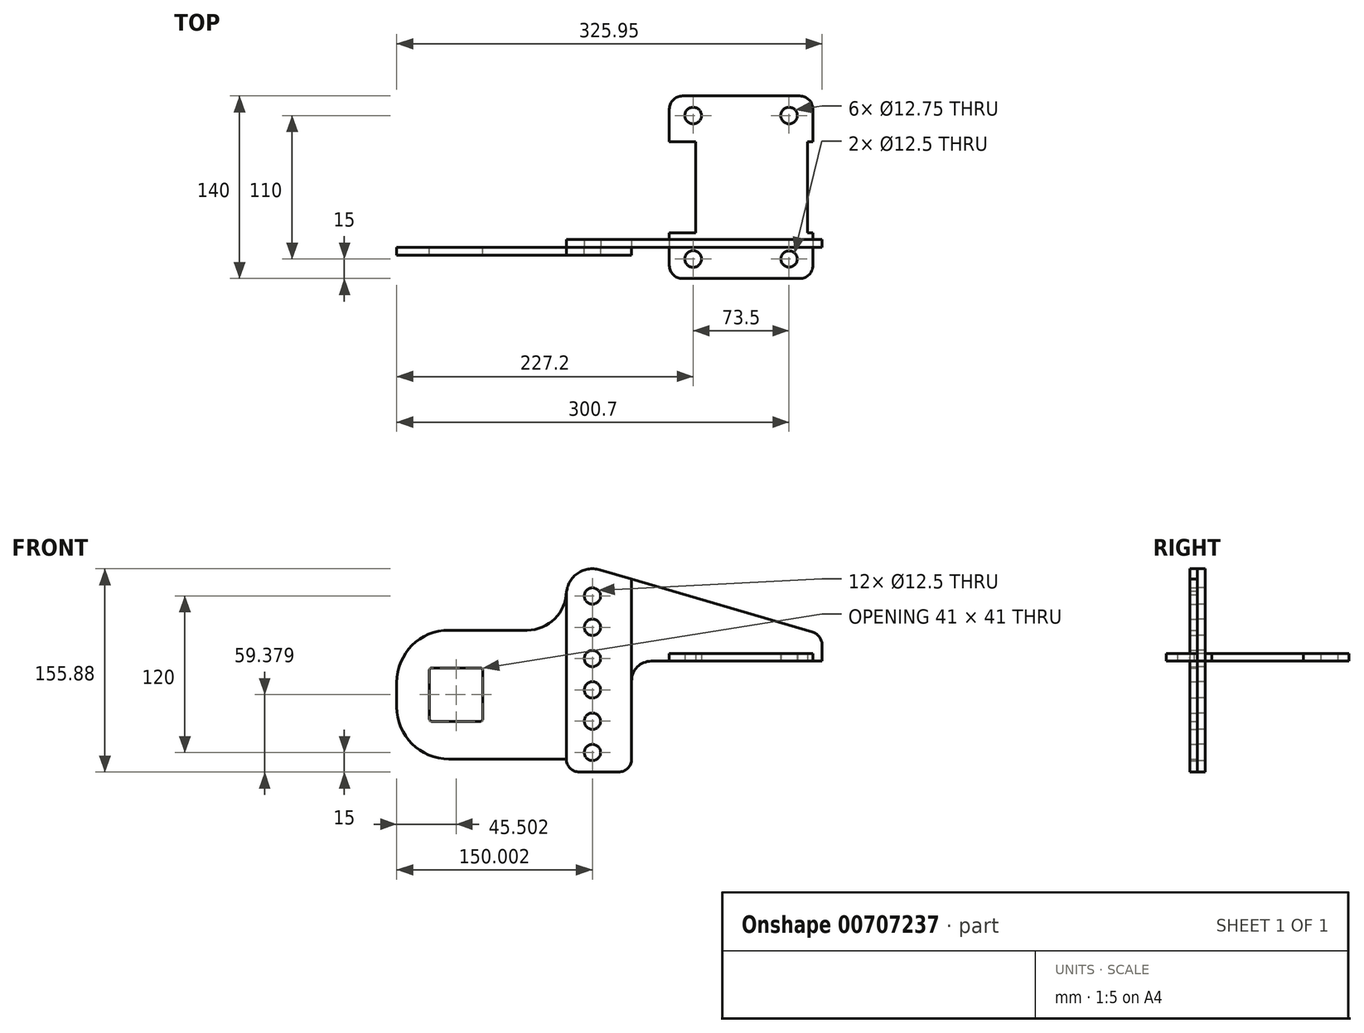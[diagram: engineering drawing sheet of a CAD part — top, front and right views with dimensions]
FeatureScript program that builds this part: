
annotation { "Feature Type Name" : "Feature", "Feature Type Description" : "" }
export const myFeature = defineFeature(function(context is Context, id is Id, definition is map)
    precondition{}
    {
        {
            var Q0;
            Q0=qCreatedBy(makeId("Top.planeOp"),FACE);
            var sketch = newSketch(context, id + "F0", { "sketchPlane" : qUnion([Q0])});
            skLineSegment(sketch, "E0.bottom", {"start": v(36.75, -55) * mm, "end": v(-36.75, -55) * mm, "construction": true});
            skLineSegment(sketch, "E0.top", {"start": v(36.75, 55) * mm, "end": v(-36.75, 55) * mm, "construction": true});
            skLineSegment(sketch, "E0.left", {"start": v(36.75, -55) * mm, "end": v(36.75, 55) * mm, "construction": true});
            skLineSegment(sketch, "E0.right", {"start": v(-36.75, -55) * mm, "end": v(-36.75, 55) * mm, "construction": true});
            skPoint(sketch, "E0.middle", {"position": v(0, 0) * mm});
            skCircle(sketch, "E1", {"center": v(-36.75, 55) * mm, "radius": 6.38 * mm});
            skCircle(sketch, "E2", {"center": v(36.75, 55) * mm, "radius": 6.38 * mm});
            skCircle(sketch, "E3", {"center": v(-36.75, -55) * mm, "radius": 6.38 * mm});
            skCircle(sketch, "E4", {"center": v(36.75, -55) * mm, "radius": 6.25 * mm});
            skLineSegment(sketch, "E5.bottom", {"start": v(45, 70) * mm, "end": v(-45, 70) * mm});
            skLineSegment(sketch, "E5.top", {"start": v(45, -70) * mm, "end": v(-45, -70) * mm});
            skLineSegment(sketch, "E5.left", {"start": v(55, 60) * mm, "end": v(55, 35) * mm});
            skLineSegment(sketch, "E5.right", {"start": v(-55, 60) * mm, "end": v(-55, 35) * mm});
            skPoint(sketch, "E6.visualSharp", {"position": v(-55, -70) * mm});
            skArc(sketch, "E6.filletArc", {"start": v(-55, -60) * mm, "mid": v(-52.07, -67.07) * mm, "end": v(-45, -70) * mm});
            skPoint(sketch, "E7.visualSharp", {"position": v(-55, 70) * mm});
            skArc(sketch, "E7.filletArc", {"start": v(-45, 70) * mm, "mid": v(-52.07, 67.07) * mm, "end": v(-55, 60) * mm});
            skPoint(sketch, "E8.visualSharp", {"position": v(55, 70) * mm});
            skArc(sketch, "E8.filletArc", {"start": v(55, 60) * mm, "mid": v(52.07, 67.07) * mm, "end": v(45, 70) * mm});
            skPoint(sketch, "E9.visualSharp", {"position": v(55, -70) * mm});
            skArc(sketch, "E9.filletArc", {"start": v(45, -70) * mm, "mid": v(52.07, -67.07) * mm, "end": v(55, -60) * mm});
            skLineSegment(sketch, "E10", {"start": v(-35, 0) * mm, "end": v(-35, -35) * mm});
            skLineSegment(sketch, "E11", {"start": v(-35, -35) * mm, "end": v(-55, -35) * mm});
            skLineSegment(sketch, "E12", {"start": v(-35, 0) * mm, "end": v(-35, 35) * mm});
            skLineSegment(sketch, "E13", {"start": v(-35, 35) * mm, "end": v(-55, 35) * mm});
            skLineSegment(sketch, "E14", {"start": v(-35, -35) * mm, "end": v(55, -35) * mm, "construction": true});
            skLineSegment(sketch, "E15", {"start": v(-35, 35) * mm, "end": v(55, 35) * mm, "construction": true});
            skLineSegment(sketch, "E16", {"start": v(55, -35) * mm, "end": v(51, -35) * mm});
            skLineSegment(sketch, "E17", {"start": v(51, -35) * mm, "end": v(51, 35) * mm});
            skLineSegment(sketch, "E18", {"start": v(51, 35) * mm, "end": v(55, 35) * mm});
            skLineSegment(sketch, "E19.trimOffspring", {"start": v(55, -35) * mm, "end": v(55, -60) * mm});
            skLineSegment(sketch, "E20.trimOffspring", {"start": v(-55, -35) * mm, "end": v(-55, -60) * mm});
            skPoint(sketch, "E21.orphan", {"position": v(-55, 0) * mm});
            skSolve(sketch);
        }
        {
            var Q0;
            Q0 = qSketchRegion(id + "F0", true);
            extrude(context, id + "F1", {"entities" : qUnion([Q0]), "depth" : 6 * mm, "offsetDistance" : 25 * mm});
        }
        {
            var Q0;
            Q0=qCreatedBy(makeId("Front.planeOp"),FACE);
            cPlane(context, id + "F2", {"entities" : qUnion([Q0]), "cplaneType" : CPlaneType.OFFSET, "offset" : 46 * mm, "width" : 150 * mm, "height" : 150 * mm});
        }
        {
            var Q0;
            Q0=qCreatedBy(id+"F2.planeOp",FACE);
            var sketch = newSketch(context, id + "F3", { "sketchPlane" : qUnion([Q0])});
            skLineSegment(sketch, "E22", {"start": v(-55, 6) * mm, "end": v(55, 6) * mm});
            skLineSegment(sketch, "E23", {"start": v(55, 6) * mm, "end": v(55, 0) * mm});
            skLineSegment(sketch, "E24", {"start": v(55, 0) * mm, "end": v(62, 0.14) * mm});
            skLineSegment(sketch, "E25", {"start": v(62, 0.14) * mm, "end": v(62, 12.65) * mm});
            skLineSegment(sketch, "E26", {"start": v(-83.95, -15) * mm, "end": v(-83.95, -75) * mm});
            skLineSegment(sketch, "E27", {"start": v(-93.95, -85) * mm, "end": v(-123.95, -85) * mm});
            skLineSegment(sketch, "E28", {"start": v(-133.95, -75) * mm, "end": v(-133.95, 50.88) * mm});
            skLineSegment(sketch, "E29", {"start": v(-108.32, 70.07) * mm, "end": v(54.81, 22.24) * mm});
            skLineSegment(sketch, "E30", {"start": v(-113.95, -85) * mm, "end": v(-113.95, 71.72) * mm, "construction": true});
            skCircle(sketch, "E31", {"center": v(-113.95, -70) * mm, "radius": 6.25 * mm});
            skCircle(sketch, "E32", {"center": v(-113.95, -46) * mm, "radius": 6.25 * mm});
            skCircle(sketch, "E33", {"center": v(-113.95, -22) * mm, "radius": 6.25 * mm});
            skCircle(sketch, "E34", {"center": v(-113.95, 2) * mm, "radius": 6.25 * mm});
            skCircle(sketch, "E35", {"center": v(-113.95, 26) * mm, "radius": 6.25 * mm});
            skCircle(sketch, "E36", {"center": v(-113.95, 50) * mm, "radius": 6.25 * mm});
            skPoint(sketch, "E37.visualSharp", {"position": v(-133.95, 77.59) * mm});
            skArc(sketch, "E37.filletArc", {"start": v(-108.32, 70.07) * mm, "mid": v(-125.94, 66.89) * mm, "end": v(-133.95, 50.88) * mm});
            skPoint(sketch, "E38.visualSharp", {"position": v(62, 20.14) * mm});
            skArc(sketch, "E38.filletArc", {"start": v(62, 12.65) * mm, "mid": v(60, 18.64) * mm, "end": v(54.81, 22.24) * mm});
            skPoint(sketch, "E39.visualSharp", {"position": v(-83.95, -85) * mm});
            skArc(sketch, "E39.filletArc", {"start": v(-93.95, -85) * mm, "mid": v(-86.88, -82.07) * mm, "end": v(-83.95, -75) * mm});
            skPoint(sketch, "E40.visualSharp", {"position": v(-133.95, -85) * mm});
            skArc(sketch, "E40.filletArc", {"start": v(-133.95, -75) * mm, "mid": v(-131.02, -82.07) * mm, "end": v(-123.95, -85) * mm});
            skLineSegment(sketch, "E41", {"start": v(-55, 0) * mm, "end": v(-68.95, 0) * mm});
            skPoint(sketch, "E42.orphan", {"position": v(-83.95, 6) * mm});
            skPoint(sketch, "E43.visualSharp", {"position": v(-83.95, 0) * mm});
            skArc(sketch, "E43.filletArc", {"start": v(-68.95, 0) * mm, "mid": v(-79.55, -4.4) * mm, "end": v(-83.95, -15) * mm});
            skLineSegment(sketch, "E44", {"start": v(-55, 6) * mm, "end": v(-55, 0) * mm});
            skSolve(sketch);
        }
        {
            var Q0;
            Q0 = qSketchRegion(id + "F3", true);
            extrude(context, id + "F4", {"entities" : qUnion([Q0]), "oppositeDirection" : true, "depth" : 6 * mm, "offsetDistance" : 25 * mm});
        }
        {
            var Q0;
            Q0 = qSketchRegion(id + "F0", true);
            extrude(context, id + "F5", {"entities" : qUnion([Q0]), "depth" : 6 * mm, "offsetDistance" : 25 * mm});
        }
        {
            var Q0;
            Q0=makeQuery(id+"F4.opExtrude","CAP_FACE",FACE,{"disambiguationData":[OSD([sQuery(id+"F3.wireOp",EDGE,"E22"),sQuery(id+"F3.wireOp",EDGE,"E23"),sQuery(id+"F3.wireOp",EDGE,"E24"),sQuery(id+"F3.wireOp",EDGE,"E25"),sQuery(id+"F3.wireOp",EDGE,"E26"),sQuery(id+"F3.wireOp",EDGE,"E27"),sQuery(id+"F3.wireOp",EDGE,"E28"),sQuery(id+"F3.wireOp",EDGE,"E29"),sQuery(id+"F3.wireOp",EDGE,"E31"),sQuery(id+"F3.wireOp",EDGE,"E32"),sQuery(id+"F3.wireOp",EDGE,"E33"),sQuery(id+"F3.wireOp",EDGE,"E34"),sQuery(id+"F3.wireOp",EDGE,"E35"),sQuery(id+"F3.wireOp",EDGE,"E36"),sQuery(id+"F3.wireOp",EDGE,"E37.filletArc"),sQuery(id+"F3.wireOp",EDGE,"E38.filletArc"),sQuery(id+"F3.wireOp",EDGE,"E39.filletArc"),sQuery(id+"F3.wireOp",EDGE,"E40.filletArc")])],"isStart":true});
            var sketch = newSketch(context, id + "F6", { "sketchPlane" : qUnion([Q0])});
            skLineSegment(sketch, "E45.0", {"start": v(-83.95, -15) * mm, "end": v(-83.95, -75) * mm});
            skPoint(sketch, "E46.0", {"position": v(-86.88, -82.07) * mm});
            skArc(sketch, "E47.0", {"start": v(-93.95, -85) * mm, "mid": v(-86.88, -82.07) * mm, "end": v(-83.95, -75) * mm});
            skLineSegment(sketch, "E48.0", {"start": v(-93.95, -85) * mm, "end": v(-123.95, -85) * mm});
            skLineSegment(sketch, "E49", {"start": v(-83.95, -15) * mm, "end": v(-83.95, 62.93) * mm});
            skLineSegment(sketch, "E50.0", {"start": v(-108.32, 70.07) * mm, "end": v(-83.95, 62.93) * mm});
            skLineSegment(sketch, "E51", {"start": v(-263.95, 10.88) * mm, "end": v(-263.95, 9.17) * mm});
            skCircle(sketch, "E52.0", {"center": v(-113.95, 26) * mm, "radius": 6.25 * mm});
            skCircle(sketch, "E53.0", {"center": v(-113.95, 2) * mm, "radius": 6.25 * mm});
            skCircle(sketch, "E54.0", {"center": v(-113.95, -22) * mm, "radius": 6.25 * mm});
            skCircle(sketch, "E55.0", {"center": v(-113.95, -46) * mm, "radius": 6.25 * mm});
            skCircle(sketch, "E56.0", {"center": v(-113.95, -70) * mm, "radius": 6.25 * mm});
            skPoint(sketch, "E57.orphan", {"position": v(-133.95, 50.88) * mm});
            skPoint(sketch, "E58.orphan", {"position": v(-108.32, 110.7) * mm});
            skPoint(sketch, "E59.orphan", {"position": v(54.81, 22.24) * mm});
            skCircle(sketch, "E60.0", {"center": v(-113.95, 50) * mm, "radius": 6.25 * mm});
            skLineSegment(sketch, "E61.bottom", {"start": v(-199.95, -5.12) * mm, "end": v(-236.95, -5.12) * mm});
            skLineSegment(sketch, "E61.top", {"start": v(-199.95, -46.12) * mm, "end": v(-236.95, -46.12) * mm});
            skLineSegment(sketch, "E61.left", {"start": v(-197.95, -7.12) * mm, "end": v(-197.95, -44.12) * mm});
            skLineSegment(sketch, "E61.right", {"start": v(-238.95, -7.12) * mm, "end": v(-238.95, -44.12) * mm});
            skPoint(sketch, "E62", {"position": v(-263.95, 9.17) * mm});
            skArc(sketch, "E63.0", {"start": v(-108.32, 70.07) * mm, "mid": v(-121.38, 69.45) * mm, "end": v(-131.27, 60.88) * mm});
            skPoint(sketch, "E64.visualSharp", {"position": v(-133.95, -75) * mm});
            skPoint(sketch, "E65.newPointB", {"position": v(-263.95, 87.34) * mm});
            skPoint(sketch, "E66.newPointB", {"position": v(-263.95, -69) * mm});
            skArc(sketch, "E66.filletArc", {"start": v(-263.95, -35) * mm, "mid": v(-252.23, -63.28) * mm, "end": v(-223.95, -75) * mm});
            skPoint(sketch, "E67.visualSharp", {"position": v(-238.95, -5.12) * mm});
            skArc(sketch, "E67.filletArc", {"start": v(-236.95, -5.12) * mm, "mid": v(-238.36, -5.7) * mm, "end": v(-238.95, -7.12) * mm});
            skPoint(sketch, "E68.visualSharp", {"position": v(-197.95, -5.12) * mm});
            skArc(sketch, "E68.filletArc", {"start": v(-197.95, -7.12) * mm, "mid": v(-198.53, -5.7) * mm, "end": v(-199.95, -5.12) * mm});
            skPoint(sketch, "E69.visualSharp", {"position": v(-197.95, -46.12) * mm});
            skArc(sketch, "E69.filletArc", {"start": v(-199.95, -46.12) * mm, "mid": v(-198.53, -45.53) * mm, "end": v(-197.95, -44.12) * mm});
            skPoint(sketch, "E70.visualSharp", {"position": v(-238.95, -46.12) * mm});
            skArc(sketch, "E70.filletArc", {"start": v(-238.95, -44.12) * mm, "mid": v(-238.36, -45.53) * mm, "end": v(-236.95, -46.12) * mm});
            skArc(sketch, "E71.0", {"start": v(-133.95, -75) * mm, "mid": v(-131.02, -82.07) * mm, "end": v(-123.95, -85) * mm});
            skLineSegment(sketch, "E72.trimOffspring", {"start": v(-133.95, -75) * mm, "end": v(-223.95, -75) * mm});
            skLineSegment(sketch, "E73", {"start": v(-83.95, -25.62) * mm, "end": v(-291.86, -25.62) * mm, "construction": true});
            skPoint(sketch, "E73.startSnap0", {"position": v(-238.95, -25.62) * mm});
            skLineSegment(sketch, "E74.MirrorCS", {"start": v(-163.95, 23.76) * mm, "end": v(-223.95, 23.76) * mm});
            skArc(sketch, "E75.MirrorCS", {"start": v(-263.95, -16.24) * mm, "mid": v(-252.23, 12.04) * mm, "end": v(-223.95, 23.76) * mm});
            skLineSegment(sketch, "E76", {"start": v(-133.95, 53.76) * mm, "end": v(-133.95, 50.88) * mm});
            skArc(sketch, "E77.0", {"start": v(-131.27, 60.88) * mm, "mid": v(-133.27, 56.06) * mm, "end": v(-133.95, 50.88) * mm});
            skPoint(sketch, "E78.visualSharp", {"position": v(-133.95, 23.76) * mm});
            skArc(sketch, "E78.filletArc", {"start": v(-163.95, 23.76) * mm, "mid": v(-142.73, 32.55) * mm, "end": v(-133.95, 53.76) * mm});
            skLineSegment(sketch, "E79.trimOffspring", {"start": v(-263.95, -16.24) * mm, "end": v(-263.95, -35) * mm});
            skSolve(sketch);
        }
        {
            var Q0;
            Q0 = qSketchRegion(id + "F6", true);
            extrude(context, id + "F7", {"entities" : qUnion([Q0]), "depth" : 6 * mm, "offsetDistance" : 25 * mm});
        }
    });
